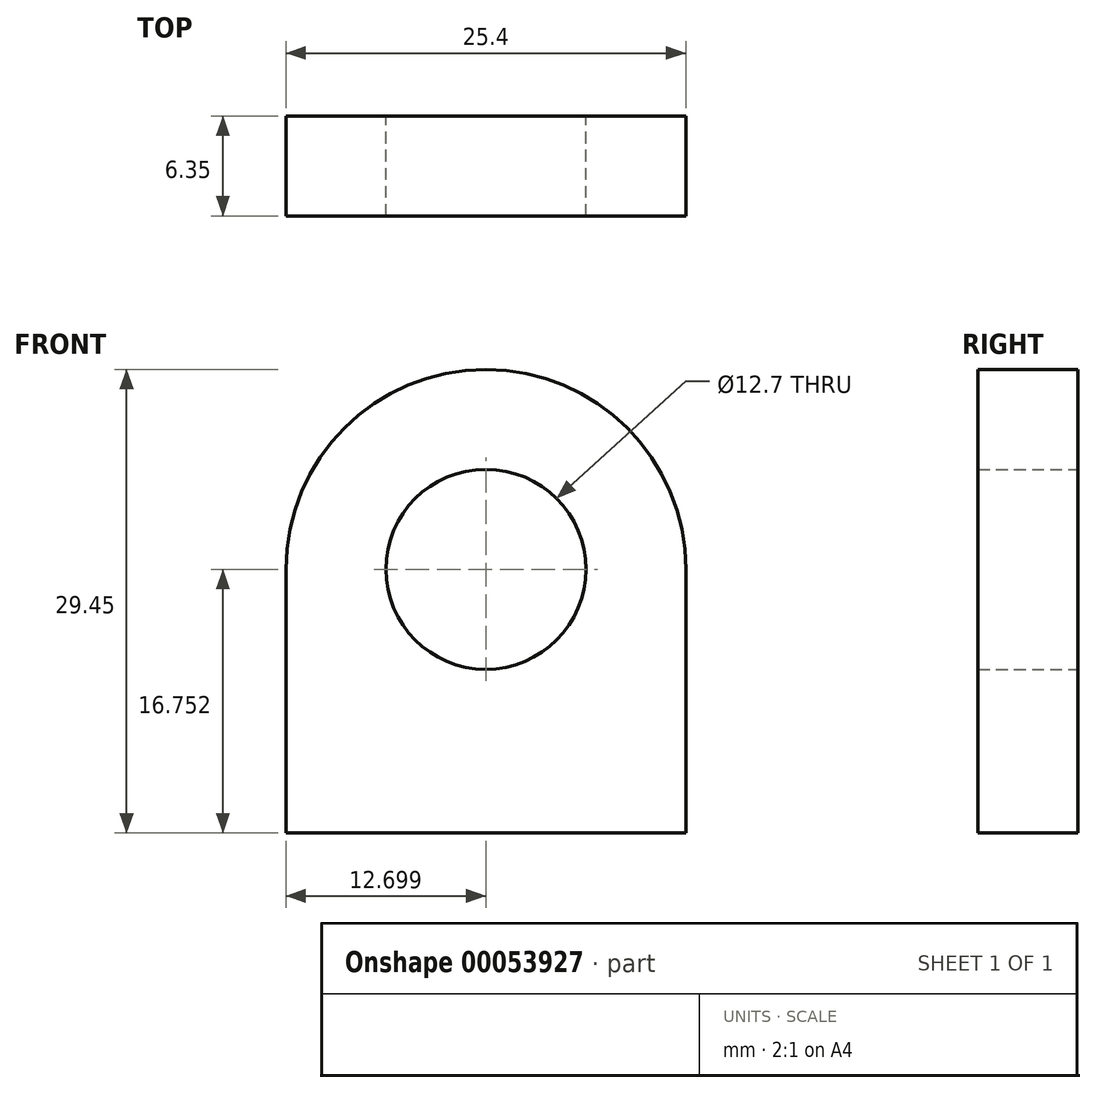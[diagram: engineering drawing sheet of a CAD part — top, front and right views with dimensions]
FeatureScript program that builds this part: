
annotation { "Feature Type Name" : "Feature", "Feature Type Description" : "" }
export const myFeature = defineFeature(function(context is Context, id is Id, definition is map)
    precondition{}
    {
        {
            var Q0;
            Q0=qCreatedBy(makeId("Front.planeOp"),FACE);
            var sketch = newSketch(context, id + "F0", { "sketchPlane" : qUnion([Q0])});
            skLineSegment(sketch, "E0.top", {"start": v(-5.45, 2.81) * mm, "end": v(19.95, 2.81) * mm});
            skLineSegment(sketch, "E0.left", {"start": v(-5.45, 19.56) * mm, "end": v(-5.45, 2.81) * mm});
            skLineSegment(sketch, "E0.right", {"start": v(19.95, 19.56) * mm, "end": v(19.95, 2.81) * mm});
            skArc(sketch, "E1", {"start": v(19.95, 19.56) * mm, "mid": v(7.25, 32.26) * mm, "end": v(-5.45, 19.56) * mm});
            skCircle(sketch, "E2", {"center": v(7.25, 19.56) * mm, "radius": 6.35 * mm});
            skSolve(sketch);
        }
        {
            var Q0;
            Q0=qSketchRegion(id+"F0",true);
            extrude(context, id + "F1", {"entities" : qUnion([Q0]), "depth" : 6.35 * mm});
        }
    });
